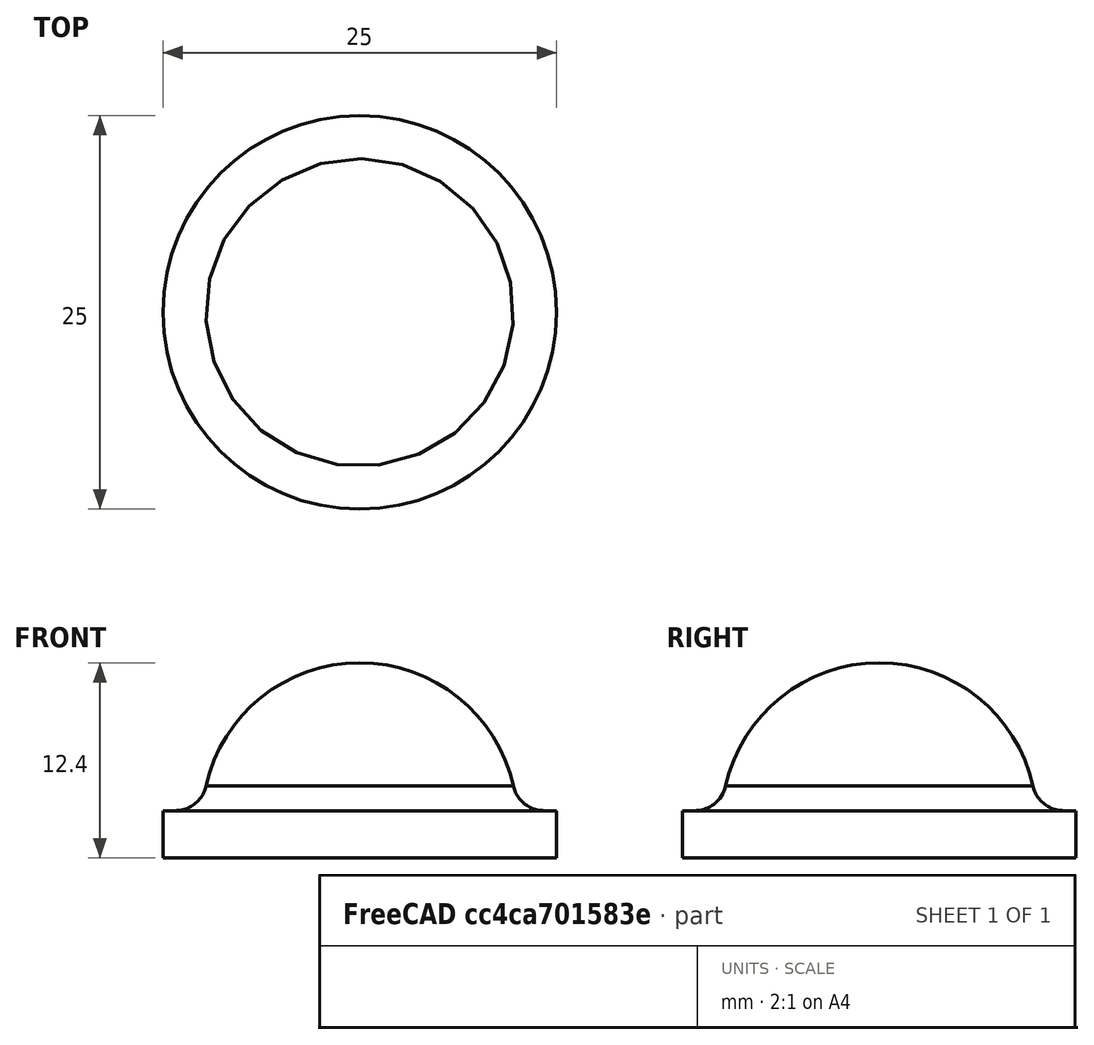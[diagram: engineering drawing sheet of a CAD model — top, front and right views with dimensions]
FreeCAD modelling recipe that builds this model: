
FCSTD DOCUMENT  (FreeCAD 0.14R2800 (Git))
Label: test-surface
License: CC-BY 3.0
LicenseURL: http://creativecommons.org/licenses/by/3.0/
objects: Sketcher::SketchObject×1, PartDesign::Pad×1, Part::Sphere×1, Part::MultiFuse×1, PartDesign::Fillet×1
note: 6 computed .brp shape members not serialized (recipe doc carries the construction recipe); baked Part::Feature solids carry a one-line shape summary decoded from their .brp

FEATURE [Sketcher::SketchObject] Sketch  label="Base"
  sketch-geometry (1):
    g0: Circle CenterX=0 CenterY=0 CenterZ=0 NormalX=0 NormalY=0 NormalZ=1 Radius=12.5
  constraints (2):
    c: Coincident(g0,g-1)
    c: Radius(g0) = 12.5
FEATURE [PartDesign::Pad] Pad  label="Base-pad"
  Length = 3
  Length2 = 100
  Sketch = -> Sketch
  Type = 0
FEATURE [Part::Sphere] Sphere
  Angle1 = -90
  Angle2 = 90
  Angle3 = 180
  Placement = pos=(0,0,2.4) rot=(1,0,0;1.5708rad)
  Radius = 10
FEATURE [Part::MultiFuse] Fusion
  Shapes = -> [Sphere,Pad]
FEATURE [PartDesign::Fillet] Fillet
  Base = -> Fusion [Edge4]
  Radius = 2
